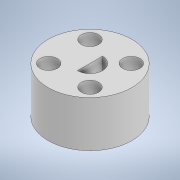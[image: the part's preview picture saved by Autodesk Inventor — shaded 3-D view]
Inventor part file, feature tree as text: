
AUTODESK INVENTOR PART (.ipt)
format: ipt  version: 2022 (Build 260153000, 153)  size: 167,424 bytes
history: native  units: mm
features: extrude x6, sketch x6, plane x1
ambient origin geometry x8: Origin, YZ Plane, XZ Plane, XY Plane, X Axis, Y Axis, Z Axis, Center Point
bodies: Solid1 (feature_tree)
feature tree (13):
  extrude  "Extrusion1"  Depth=7.0mm TaperAngle=0.0deg
  extrude  "Extrusion2"  Depth=4.0mm TaperAngle=0.0deg
  extrude  "Extrusion3"  Depth=2.25mm
  plane  "Work Plane1"
  extrude  "Extrusion4"  Depth=3.0mm
  extrude  "Extrusion5"  Depth=3.0mm
  extrude  "Extrusion6"  Depth=4.0mm
  sketch  "Sketch1"  dims[d0=20.0mm d1=7.0mm d2=0.0mm]
  sketch  "Sketch2"  dims[d3=6.0mm d4=4.0mm d5=0.0mm]
  sketch  "Sketch3"  dims[d6=1.0mm d7=0.0mm d9=2.25mm]
  sketch  "Sketch4"  dims[d10=1.0mm d11=0.0mm d14=3.0mm]
  sketch  "Sketch5"  dims[d15=40.0mm d17=360.0deg d19=3.0mm]
  sketch  "Sketch6"  dims[d20=0.0mm d21=4.15mm d22=4.0mm d23=0.0mm]
